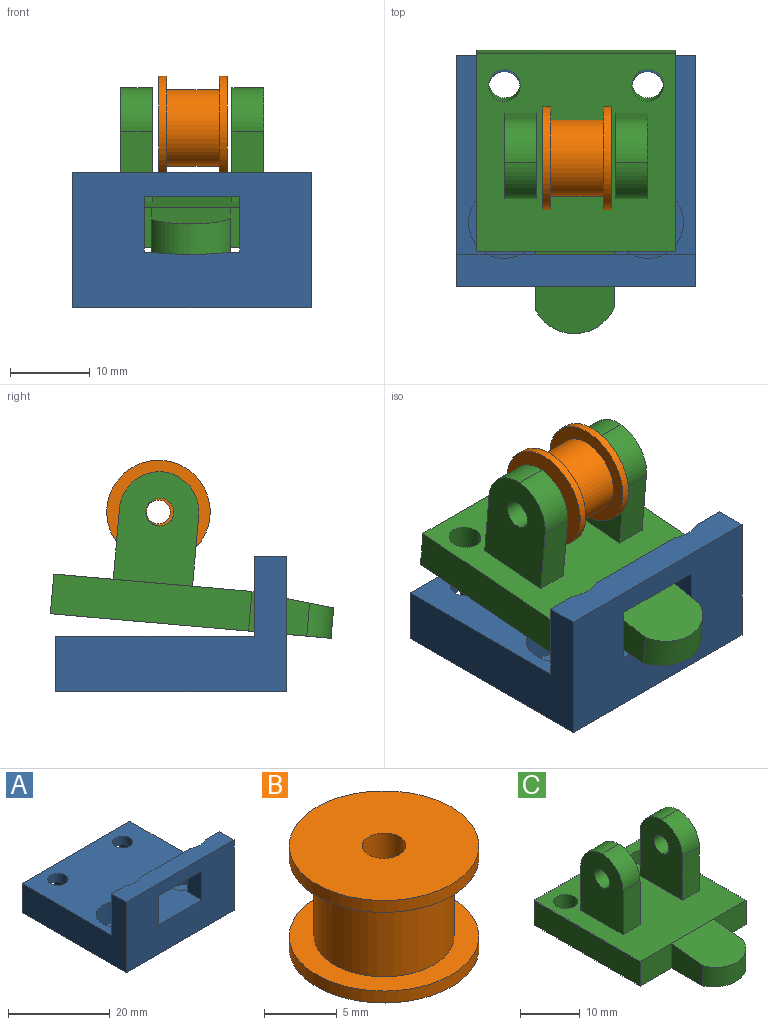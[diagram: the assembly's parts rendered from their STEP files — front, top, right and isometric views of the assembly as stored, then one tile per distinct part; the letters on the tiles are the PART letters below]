
ASSEMBLY  parts=3 mates=1
PART A: 39 faces, bbox 30x29x17 mm
  f0: plane 30x17mm, normal (0,-1,0), area 426mm2, adj f2,f7,f8,f9,f21,f36,f37,f38
  f1: plane 30x7mm, normal (0,1,0), area 174mm2, adj f2,f7,f8,f9,f22,f23,f24,f25
  f2: plane 30x29mm, normal (0,0,1), area 648.4mm2, adj f0,f1,f7,f8,f10,f13,f16,f18
  f3: plane 4.12x0.5mm, normal (0,0,1), area 1.4mm2, adj f11,f19
  f4: plane 4.12x0.5mm, normal (0,0,1), area 1.4mm2, adj f14,f17
  f5: cylinder r=2.75mm len=5.5mm, axis (0,0,1), area 34.6mm2, adj f9,f15
  f6: cylinder r=2.75mm len=5.5mm, axis (0,0,1), area 34.6mm2, adj f9,f12
  f7: plane 29x17mm, normal (-1,0,0), area 243mm2, adj f0,f1,f2,f9,f20,f21
  f8: plane 29x17mm, normal (1,0,0), area 243mm2, adj f0,f1,f2,f9,f16,f21
  f9: plane 30x29mm, normal (0,0,-1), area 797.4mm2, adj f0,f1,f5,f6,f7,f8,f33,f35
  f10: cylinder r=4.5mm len=9mm, axis (0,0,1), area 120mm2, adj f2,f11,f12
  f11: plane 5x4.12mm, normal (0,1,0), area 20.6mm2, adj f3,f10,f12
  f12: plane 9x8.5mm, normal (0,0,1), area 38.5mm2, adj f6,f10,f11
  f13: cylinder r=4.5mm len=9mm, axis (0,0,1), area 120mm2, adj f2,f14,f15
  f14: plane 5x4.12mm, normal (0,1,0), area 20.6mm2, adj f4,f13,f15
  f15: plane 9x8.5mm, normal (0,0,1), area 38.5mm2, adj f5,f13,f14
  f16: plane 10x3.94mm, normal (0,1,0), area 39.4mm2, adj f2,f8,f17,f21
  f17: cylinder r=4.5mm len=10mm, axis (0,0,-1), area 42.8mm2, adj f4,f16,f18,f21
  f18: plane 13.88x10mm, normal (0,1,0), area 54.8mm2, adj f2,f17,f19,f21,f36,f37,f38
  f19: cylinder r=4.5mm len=10mm, axis (0,0,-1), area 42.8mm2, adj f3,f18,f20,f21
  f20: plane 10x3.94mm, normal (0,1,0), area 39.4mm2, adj f2,f7,f19,f21
  f21: plane 30x4mm, normal (0,0,1), area 117.2mm2, adj f0,f7,f8,f16,f17,f18,f19,f20
  f22: plane 6.7x6mm, normal (0,0,1), area 27.6mm2, adj f1,f23,f25,f26,f35
  f23: plane 6.7x3mm, normal (1,0,0), area 20.1mm2, adj f1,f22,f24,f26
  f24: plane 6.7x6mm, normal (0,0,-1), area 27.6mm2, adj f1,f23,f25,f26,f34
  f25: plane 6.7x3mm, normal (-1,0,0), area 20.1mm2, adj f1,f22,f24,f26
  f26: plane 6x3mm, normal (0,1,0), area 18mm2, adj f22,f23,f24,f25
  f27: plane 6.7x6mm, normal (0,0,1), area 27.6mm2, adj f1,f28,f30,f31,f33
  f28: plane 6.7x3mm, normal (1,0,0), area 20.1mm2, adj f1,f27,f29,f31
  f29: plane 6.7x6mm, normal (0,0,-1), area 27.6mm2, adj f1,f28,f30,f31,f32
  f30: plane 6.7x3mm, normal (-1,0,0), area 20.1mm2, adj f1,f27,f29,f31
  f31: plane 6x3mm, normal (0,1,0), area 18mm2, adj f27,f28,f29,f30
  f32: cylinder r=2mm len=4mm, axis (0,0,-1), area 25.1mm2, adj f2,f29
  f33: cylinder r=2mm len=4mm, axis (0,0,-1), area 25.1mm2, adj f9,f27
  f34: cylinder r=2mm len=4mm, axis (0,0,-1), area 25.1mm2, adj f2,f24
  f35: cylinder r=2mm len=4mm, axis (0,0,-1), area 25.1mm2, adj f9,f22
  f36: plane 7x4mm, normal (1,0,0), area 28mm2, adj f0,f2,f18,f38
  f37: plane 7x4mm, normal (-1,0,0), area 28mm2, adj f0,f2,f18,f38
  f38: plane 12x4mm, normal (0,0,-1), area 48mm2, adj f0,f18,f36,f37
PART B: 8 faces, bbox 13x13x8.6 mm
  f0: cylinder r=6.5mm len=13mm, axis (0,0,-1), area 40.8mm2, adj f4,f7
  f1: cylinder r=6.5mm len=13mm, axis (0,0,-1), area 40.8mm2, adj f3,f6
  f2: cylinder r=1.5mm len=8.6mm, axis (0,0,-1), area 81.1mm2, adj f3,f4
  f3: plane 13x13mm, normal (0,0,1), area 125.7mm2, adj f1,f2
  f4: plane 13x13mm, normal (0,0,-1), area 125.7mm2, adj f0,f2
  f5: cylinder r=4.8mm len=9.6mm, axis (0,0,-1), area 199.1mm2, adj f6,f7
  f6: plane 13x13mm, normal (0,0,-1), area 60.3mm2, adj f1,f5
  f7: plane 13x13mm, normal (0,0,1), area 60.3mm2, adj f0,f5
PART C: 27 faces, bbox 25x35.4x19 mm
  f0: plane 25x25mm, normal (0,0,1), area 519.9mm2, adj f4,f5,f6,f7,f8,f10,f11,f12
  f1: plane 7.34x5mm, normal (-1,0,0), area 33.6mm2, adj f2,f6,f9,f10
  f2: cylinder r=5.44mm len=10mm, axis (0,0,-1), area 50.2mm2, adj f1,f3,f9,f10
  f3: plane 6.85x5mm, normal (1,0,0), area 31.6mm2, adj f2,f7,f9,f10
  f4: plane 25x5mm, normal (0,1,0), area 125mm2, adj f0,f5,f8,f9
  f5: plane 25x5mm, normal (-1,0,0), area 125mm2, adj f0,f4,f6,f9
  f6: plane 7.36x5mm, normal (0,-1,0), area 36.8mm2, adj f0,f1,f5,f9
  f7: plane 7.64x5mm, normal (0,-1,0), area 38.2mm2, adj f0,f3,f8,f9
  f8: plane 25x5mm, normal (1,0,0), area 125mm2, adj f0,f4,f7,f9
  f9: plane 35.41x25mm, normal (0,0,-1), area 694.7mm2, adj f1,f2,f3,f4,f5,f6,f7,f8
  f10: plane 10.41x10mm, normal (0,-0.11,0.99), area 95.5mm2, adj f0,f1,f2,f3
  f11: cylinder r=2mm len=5mm, axis (0,0,1), area 62.8mm2, adj f0,f9
  f12: cylinder r=2mm len=5mm, axis (0,0,1), area 62.8mm2, adj f0,f9
  f13: plane 8.92x4mm, normal (0,1,0), area 35.7mm2, adj f0,f14,f16,f23
  f14: plane 14x10mm, normal (-1,0,0), area 119.3mm2, adj f0,f13,f15,f23,f24,f26
  f15: plane 8.92x4mm, normal (0,-1,0), area 35.7mm2, adj f0,f14,f16,f24
  f16: plane 14x10mm, normal (1,0,0), area 119.3mm2, adj f0,f13,f15,f23,f24,f26
  f17: plane 8.92x4mm, normal (0,1,0), area 35.7mm2, adj f0,f18,f20,f21
  f18: plane 14x10mm, normal (-1,0,0), area 119.3mm2, adj f0,f17,f19,f21,f22,f25
  f19: plane 8.92x4mm, normal (0,-1,0), area 35.7mm2, adj f0,f18,f20,f22
  f20: plane 14x10mm, normal (1,0,0), area 119.3mm2, adj f0,f17,f19,f21,f22,f25
  f21: cylinder r=5.08mm len=5.08mm, axis (1,0,0), area 31.6mm2, adj f17,f18,f20,f22
  f22: cylinder r=5.08mm len=5.08mm, axis (-1,0,0), area 31.6mm2, adj f18,f19,f20,f21
  f23: cylinder r=5.08mm len=5.08mm, axis (1,0,0), area 31.6mm2, adj f13,f14,f16,f24
  f24: cylinder r=5.08mm len=5.08mm, axis (-1,0,0), area 31.6mm2, adj f14,f15,f16,f23
  f25: cylinder r=1.75mm len=4mm, axis (-1,0,0), area 44mm2, adj f18,f20
  f26: cylinder r=1.75mm len=4mm, axis (-1,0,0), area 44mm2, adj f14,f16
PLACE A t=(0.08,1.29,-12.23)mm
PLACE B rot(axis=(0.04,1,0.04),90.1deg) t=(-4.1,9.36,19.36)mm
PLACE C rot(axis=(1,0,0),5deg) t=(0.1,10.67,3.49)mm
MATE fastened B.f2 <-> C.f22  axis (1,0,0) through (-4.1,9.36,19.36)mm
